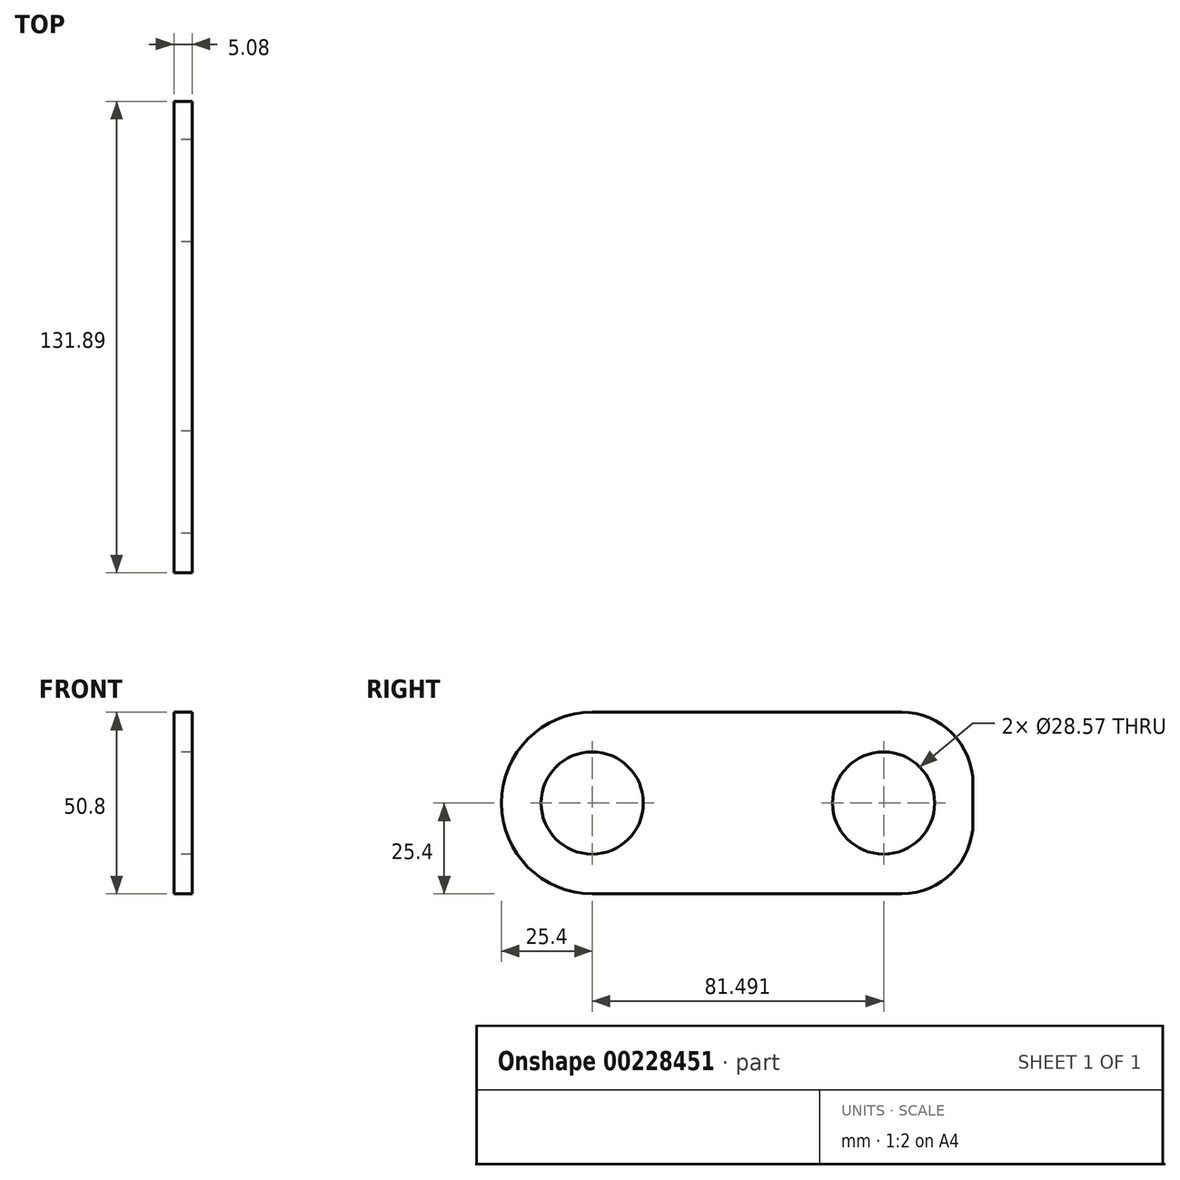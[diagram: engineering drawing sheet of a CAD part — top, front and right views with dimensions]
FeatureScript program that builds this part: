
annotation { "Feature Type Name" : "Feature", "Feature Type Description" : "" }
export const myFeature = defineFeature(function(context is Context, id is Id, definition is map)
    precondition{}
    {
        {
            var Q0;
            Q0=qCreatedBy(makeId("Right.planeOp"),FACE);
            var sketch = newSketch(context, id + "F0", { "sketchPlane" : qUnion([Q0])});
            skArc(sketch, "E0", {"start": v(0, 25.4) * mm, "mid": v(-25.4, 0) * mm, "end": v(0, -25.4) * mm});
            skLineSegment(sketch, "E1", {"start": v(0, 25.4) * mm, "end": v(86.5, 25.4) * mm});
            skLineSegment(sketch, "E2", {"start": v(0, -25.4) * mm, "end": v(86.5, -25.4) * mm});
            skLineSegment(sketch, "E3", {"start": v(106.5, 5.4) * mm, "end": v(106.5, -5.4) * mm});
            skCircle(sketch, "E4", {"center": v(0, 0) * mm, "radius": 14.29 * mm});
            skCircle(sketch, "E5", {"center": v(81.5, 0) * mm, "radius": 14.29 * mm});
            skPoint(sketch, "E6.visualSharp", {"position": v(106.5, 25.4) * mm});
            skArc(sketch, "E6.filletArc", {"start": v(106.5, 5.4) * mm, "mid": v(100.63, 19.54) * mm, "end": v(86.5, 25.4) * mm});
            skPoint(sketch, "E7.visualSharp", {"position": v(106.5, -25.4) * mm});
            skArc(sketch, "E7.filletArc", {"start": v(86.5, -25.4) * mm, "mid": v(100.63, -19.54) * mm, "end": v(106.5, -5.4) * mm});
            skSolve(sketch);
        }
        {
            var Q0;
            Q0=makeQuery(id+"F0.imprint","IMPRINT",FACE,{"disambiguationData":[TD([[makeQuery(id+"F0.imprint","IMPRINT",EDGE,{"derivedFrom":sQuery(id+"F0.wireOp",EDGE,"E0")}),1.0]])]});
            extrude(context, id + "F1", {"entities" : qUnion([Q0]), "depth" : 5.08 * mm});
        }
    });
